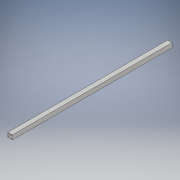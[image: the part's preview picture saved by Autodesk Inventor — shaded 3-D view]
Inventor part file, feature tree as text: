
AUTODESK INVENTOR PART (.ipt)
format: ipt  version: 2018 (Build 220112000, 112)  size: 98,304 bytes
history: native  units: in
note: dims shown in document units (in); Inventor stores cm internally (conversion verified against a paired STEP export)
features: extrude x1, sketch x1
ambient origin geometry x8: Origin, YZ Plane, XZ Plane, XY Plane, X Axis, Y Axis, Z Axis, Center Point
bodies: Solid1 (feature_tree)
feature tree (2):
  extrude  "Extrusion1"  Depth=1.0in
  sketch  "Sketch1"  dims[d0=1.0in d1=1.0in d2=0.125in d3=36.0in d4=0.0in]
